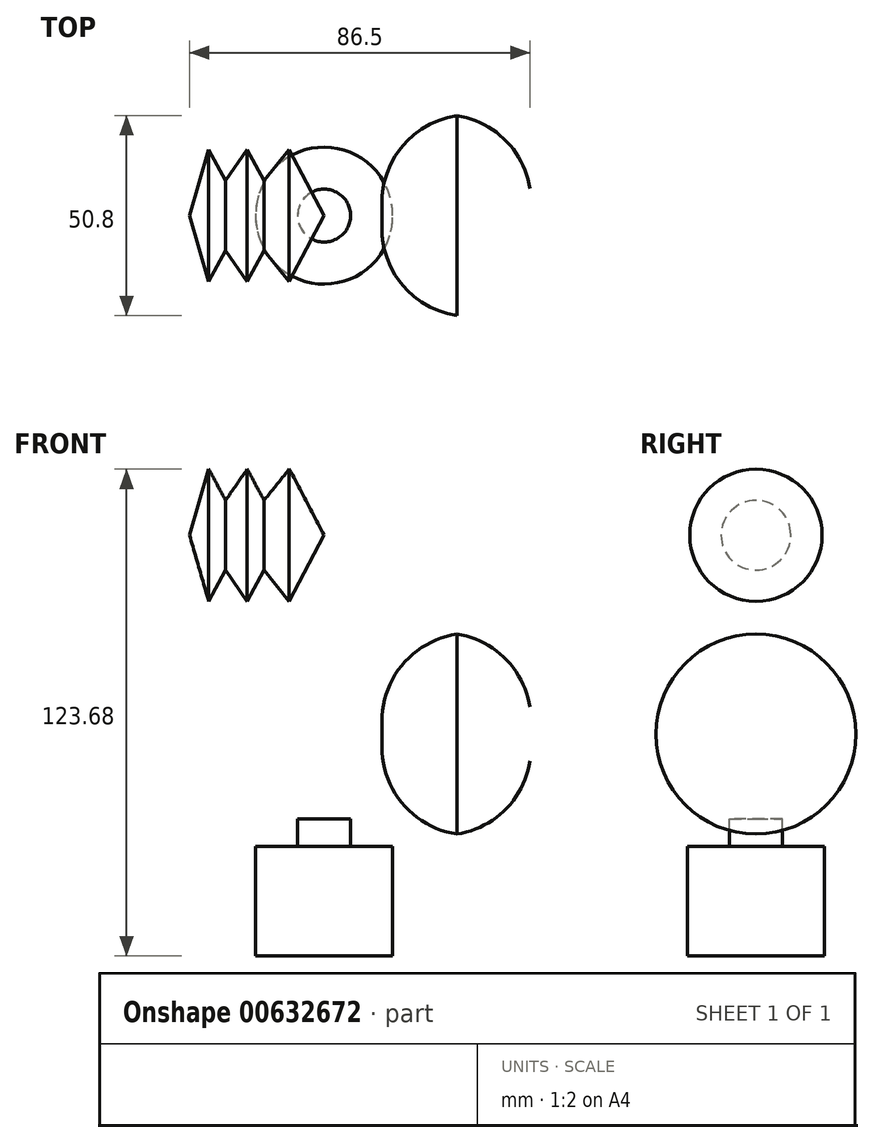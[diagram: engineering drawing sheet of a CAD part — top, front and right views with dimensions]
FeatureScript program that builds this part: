
annotation { "Feature Type Name" : "Feature", "Feature Type Description" : "" }
export const myFeature = defineFeature(function(context is Context, id is Id, definition is map)
    precondition{}
    {
        {
            var Q0;
            Q0=qCreatedBy(makeId("Front.planeOp"),FACE);
            var sketch = newSketch(context, id + "F0", { "sketchPlane" : qUnion([Q0])});
            skLineSegment(sketch, "E0", {"start": v(0, 0) * mm, "end": v(-25.4, 0) * mm});
            skLineSegment(sketch, "E1", {"start": v(0, 0) * mm, "end": v(25.4, 0) * mm});
            skLineSegment(sketch, "E2", {"start": v(0, 0) * mm, "end": v(0, 25.4) * mm});
            skArc(sketch, "E3", {"start": v(0, 25.4) * mm, "mid": v(-19.15, 19.15) * mm, "end": v(-25.4, 0) * mm});
            skArc(sketch, "E4", {"start": v(25.4, 0) * mm, "mid": v(19.1, 19.1) * mm, "end": v(0, 25.4) * mm});
            skSolve(sketch);
        }
        {
            var Q0;
            Q0 = qSketchRegion(id + "F0", true);
            var Q1;
            Q1=sQuery(id+"F0.wireOp",EDGE,"E1");
            revolve(context, id + "F1", {"entities" : qUnion([Q0]), "axis" : qUnion([Q1]), "revolveType" : RevolveType.FULL});
        }
        {
            var Q0;
            Q0=qCreatedBy(makeId("Front.planeOp"),FACE);
            var sketch = newSketch(context, id + "F2", { "sketchPlane" : qUnion([Q0])});
            skLineSegment(sketch, "E5", {"start": v(-67.95, 50.54) * mm, "end": v(-33.74, 50.54) * mm});
            skLineSegment(sketch, "E6", {"start": v(-33.74, 50.54) * mm, "end": v(-42.6, 67.34) * mm});
            skLineSegment(sketch, "E7", {"start": v(-42.6, 67.34) * mm, "end": v(-49.01, 59.4) * mm});
            skLineSegment(sketch, "E8", {"start": v(-49.01, 59.4) * mm, "end": v(-53.29, 67.34) * mm});
            skLineSegment(sketch, "E9", {"start": v(-53.29, 67.34) * mm, "end": v(-58.79, 59.4) * mm});
            skLineSegment(sketch, "E10", {"start": v(-58.79, 59.4) * mm, "end": v(-63.06, 67.34) * mm});
            skLineSegment(sketch, "E11", {"start": v(-63.06, 67.34) * mm, "end": v(-67.95, 50.54) * mm});
            skSolve(sketch);
        }
        {
            var Q0;
            Q0 = qSketchRegion(id + "F2", true);
            var Q1;
            Q1=sQuery(id+"F2.wireOp",EDGE,"E5");
            revolve(context, id + "F3", {"entities" : qUnion([Q0]), "axis" : qUnion([Q1]), "revolveType" : RevolveType.FULL});
        }
        {
            var Q0;
            Q0=qCreatedBy(makeId("Front.planeOp"),FACE);
            var sketch = newSketch(context, id + "F4", { "sketchPlane" : qUnion([Q0])});
            skLineSegment(sketch, "E12", {"start": v(-33.74, -56.34) * mm, "end": v(-51.15, -56.34) * mm});
            skLineSegment(sketch, "E13", {"start": v(-51.15, -56.34) * mm, "end": v(-51.15, -28.55) * mm});
            skLineSegment(sketch, "E14", {"start": v(-51.15, -28.55) * mm, "end": v(-40.46, -28.55) * mm});
            skLineSegment(sketch, "E15", {"start": v(-40.46, -28.55) * mm, "end": v(-40.46, -21.53) * mm});
            skLineSegment(sketch, "E16", {"start": v(-40.46, -21.53) * mm, "end": v(-33.74, -21.53) * mm});
            skLineSegment(sketch, "E17", {"start": v(-33.74, -21.53) * mm, "end": v(-33.74, -56.34) * mm});
            skSolve(sketch);
        }
        {
            var Q0;
            Q0 = qSketchRegion(id + "F4", true);
            var Q1;
            Q1=sQuery(id+"F4.wireOp",EDGE,"E17");
            revolve(context, id + "F5", {"entities" : qUnion([Q0]), "axis" : qUnion([Q1]), "revolveType" : RevolveType.FULL});
        }
    });
